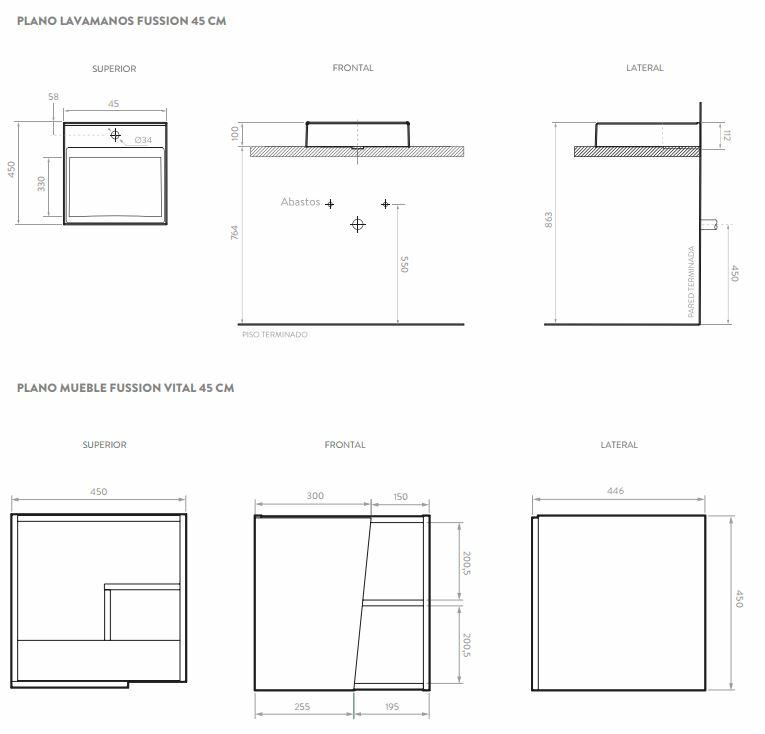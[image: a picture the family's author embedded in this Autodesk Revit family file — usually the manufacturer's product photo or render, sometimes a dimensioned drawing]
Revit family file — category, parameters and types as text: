
# Revit family: LM0056101_Mueble Fussion Vital 45 cm con Lavamanos
name_source: partatom
category: Plumbing Fixtures
units: mm (PartAtom-declared; Revit-internal decimal feet)

## family parameters
Always vertical = Yes
Cut with Voids When Loaded = No
Host = Wall
OmniClass Number = 23.45.00.00
OmniClass Title = Sanitary, Laundry, and Cleaning Equipment
Part Type = Normal
Room Calculation Point = No
Round Connector Dimension = Use Diameter
Shared = No

## types (1)
- Type 1
    Alto = 1064 mm  [stored 3.49081 ft]
    Ancho = 450 mm  [stored 1.47638 ft]
    Capacidad de carga = 88,2 lb (40 kg)
    Creado por = IDD
    Densidad = 15mm 670 kg./m^3
    Dimensiones generales producto (H * W * D) = 17,72” x 17,72” x 17,56” (450,0 x 450 x 446 mm)
    Fabricante = Corona
    Fecha de creación = 24/07/2020
    Garantía = 5 años
    Material = Corona_Madera_Aglomerada_Duna
    Peso Bruto aprox = 24 lb (10,9 kg)
    Peso Neto aprox = 22,5 lb (10,2 kg)
    Profundidad = 450 mm  [stored 1.47638 ft]
    Referencia = LM0056101
    URL = https://corona.co

note: [stored X ft] marks values corroborated as IEEE doubles in the binary element streams (Revit-internal decimal feet)

## geometry (parser evidence)
native form markers: Sweep x5
no freeform markers — native parametric forms only
